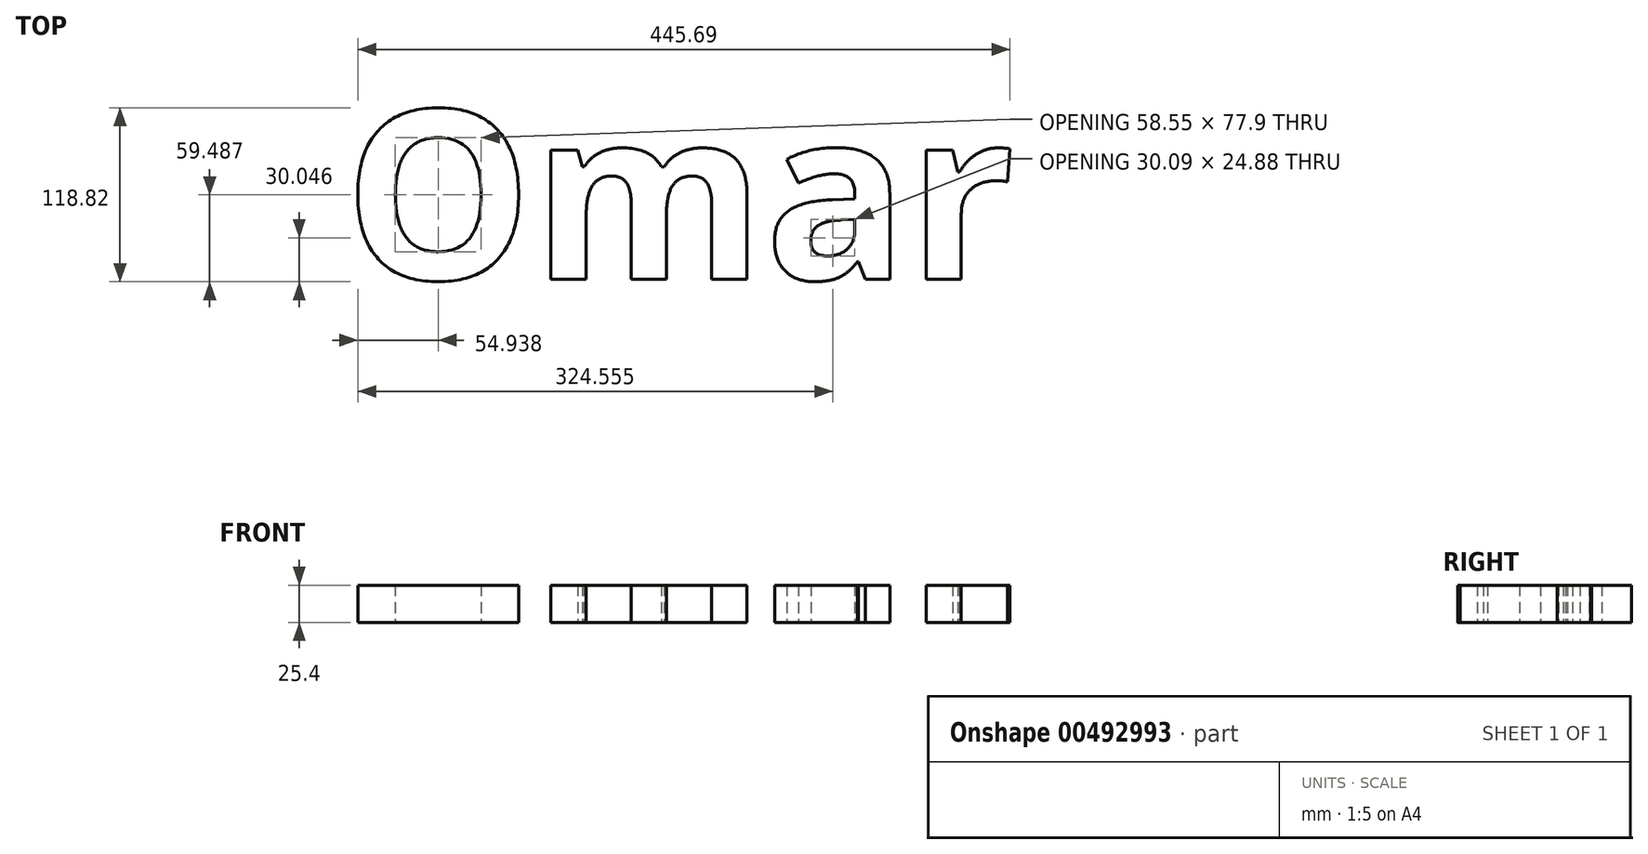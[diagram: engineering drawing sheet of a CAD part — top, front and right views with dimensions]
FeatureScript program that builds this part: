
annotation { "Feature Type Name" : "Feature", "Feature Type Description" : "" }
export const myFeature = defineFeature(function(context is Context, id is Id, definition is map)
    precondition{}
    {
        {
            var Q0;
            Q0=qCreatedBy(makeId("Top.planeOp"),FACE);
            var sketch = newSketch(context, id + "F0", { "sketchPlane" : qUnion([Q0])});
            skText(sketch, "E0", { "text": "Omar", "fontName": "OpenSans-Bold.ttf"});
            const initialGuessF0  = {"E0": [-0.19223, -0.0385, 1, 0, 0.1164]};
            skSetInitialGuess(sketch, initialGuessF0);
            skSolve(sketch);
        }
        {
            var Q0;
            Q0 = qSketchRegion(id + "F0", true);
            extrude(context, id + "F1", {"entities" : qUnion([Q0]), "depth" : 25.4 * mm});
        }
    });
